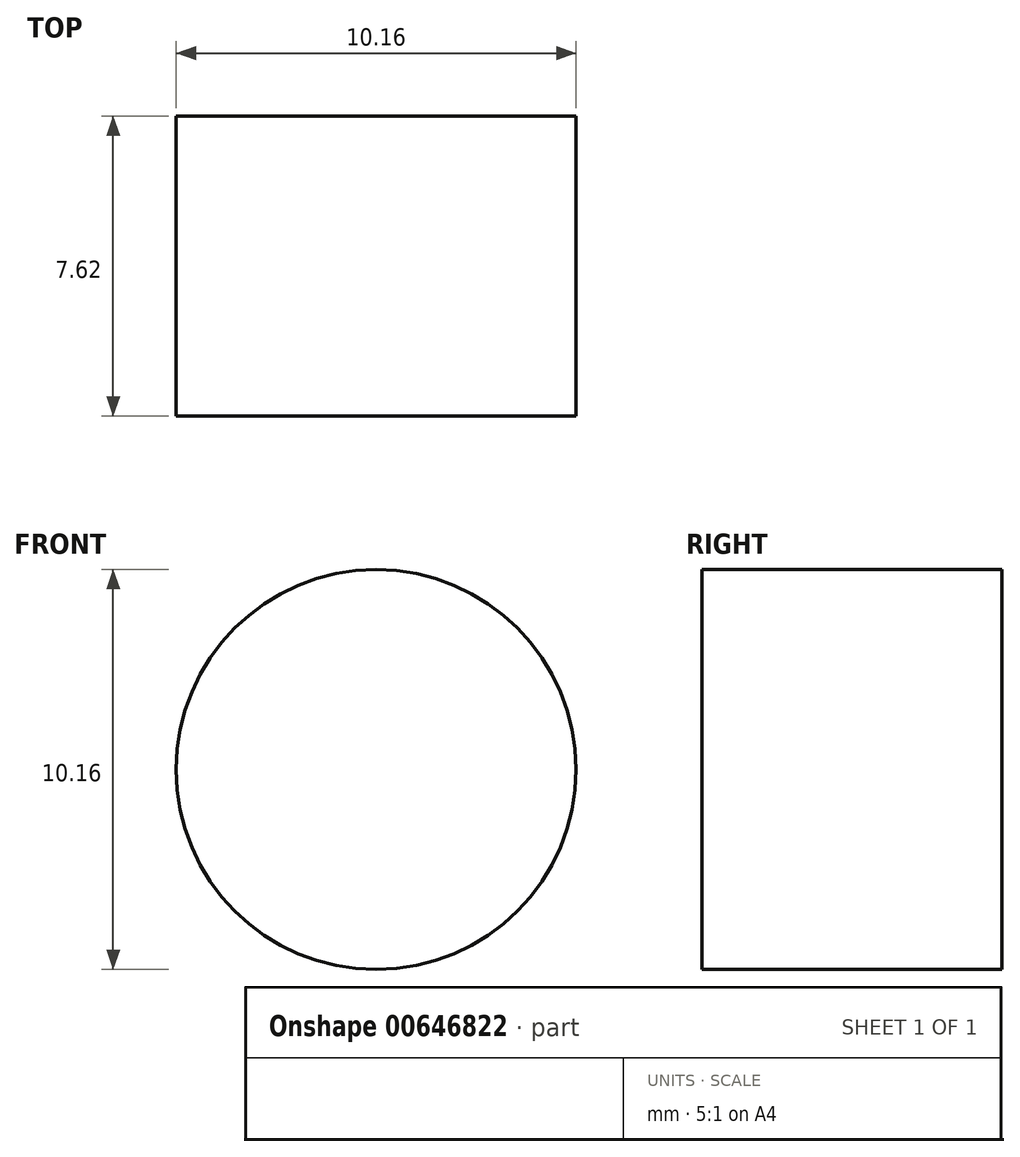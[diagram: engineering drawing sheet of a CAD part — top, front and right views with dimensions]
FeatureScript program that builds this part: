
annotation { "Feature Type Name" : "Feature", "Feature Type Description" : "" }
export const myFeature = defineFeature(function(context is Context, id is Id, definition is map)
    precondition{}
    {
        {
            var Q0;
            Q0=qCreatedBy(makeId("Front.planeOp"),FACE);
            var sketch = newSketch(context, id + "F0", { "sketchPlane" : qUnion([Q0])});
            skCircle(sketch, "E0", {"center": v(-23.11, 13.87) * mm, "radius": 5.08 * mm});
            skSolve(sketch);
        }
        {
            var Q0;
            Q0=makeQuery(id+"F0.imprint","IMPRINT",FACE,{"disambiguationData":[TD([[makeQuery(id+"F0.imprint","IMPRINT",EDGE,{"derivedFrom":sQuery(id+"F0.wireOp",EDGE,"E0")}),1.0]])]});
            extrude(context, id + "F1", {"entities" : qUnion([Q0]), "depth" : 7.62 * mm, "offsetDistance" : 25.4 * mm});
        }
    });
